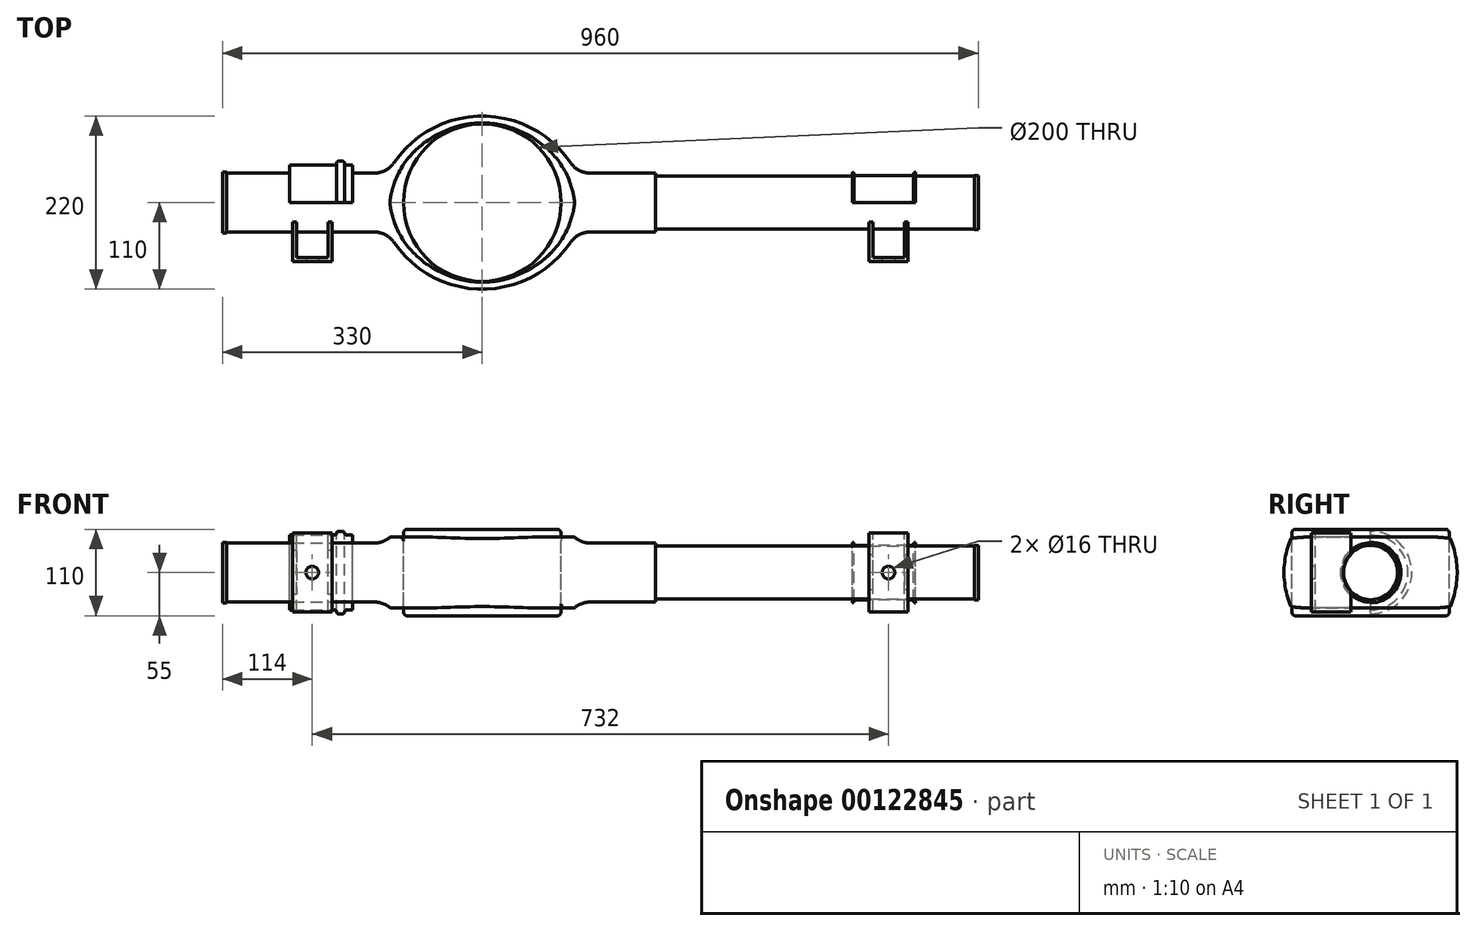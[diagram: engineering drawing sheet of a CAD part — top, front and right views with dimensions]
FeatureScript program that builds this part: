
annotation { "Feature Type Name" : "Feature", "Feature Type Description" : "" }
export const myFeature = defineFeature(function(context is Context, id is Id, definition is map)
    precondition{}
    {
        {
            var Q0;
            Q0=qCreatedBy(makeId("Front.planeOp"),FACE);
            var sketch = newSketch(context, id + "F0", { "sketchPlane" : qUnion([Q0])});
            skLineSegment(sketch, "E0", {"start": v(0, 0) * mm, "end": v(480, 0) * mm, "construction": true});
            skLineSegment(sketch, "E1", {"start": v(0, 0) * mm, "end": v(-480, 0) * mm, "construction": true});
            skLineSegment(sketch, "E2", {"start": v(-480, 0) * mm, "end": v(-480, 38.5) * mm});
            skLineSegment(sketch, "E3", {"start": v(-480, 38.5) * mm, "end": v(-475, 38.5) * mm});
            skLineSegment(sketch, "E4", {"start": v(-475, 38.5) * mm, "end": v(-475, 37.5) * mm});
            skLineSegment(sketch, "E5", {"start": v(-475, 37.5) * mm, "end": v(-395, 37.5) * mm});
            skLineSegment(sketch, "E6", {"start": v(-395, 37.5) * mm, "end": v(-395, 47.5) * mm});
            skLineSegment(sketch, "E7", {"start": v(-395, 47.5) * mm, "end": v(-337.5, 47.5) * mm});
            skLineSegment(sketch, "E8", {"start": v(-335, 50) * mm, "end": v(-335, 50) * mm});
            skLineSegment(sketch, "E9", {"start": v(-332.5, 52.5) * mm, "end": v(-327.5, 52.5) * mm});
            skLineSegment(sketch, "E10", {"start": v(-325, 50) * mm, "end": v(-325, 50) * mm});
            skLineSegment(sketch, "E11", {"start": v(-322.5, 47.5) * mm, "end": v(-315, 47.5) * mm});
            skLineSegment(sketch, "E12", {"start": v(-315, 47.5) * mm, "end": v(-315, 37.5) * mm});
            skLineSegment(sketch, "E13", {"start": v(-315, 37.5) * mm, "end": v(-286.93, 37.5) * mm});
            skLineSegment(sketch, "E14", {"start": v(-270, 37.5) * mm, "end": v(-30, 37.5) * mm});
            skPoint(sketch, "E15", {"position": v(-150, 110) * mm});
            skArc(sketch, "E16", {"start": v(-37.88, 50.64) * mm, "mid": v(-150, 110) * mm, "end": v(-262.12, 50.64) * mm});
            skPoint(sketch, "E17.visualSharp", {"position": v(-270, 37.5) * mm});
            skArc(sketch, "E17.filletArc", {"start": v(-286.93, 37.5) * mm, "mid": v(-272.9, 40.99) * mm, "end": v(-262.12, 50.64) * mm});
            skLineSegment(sketch, "E18", {"start": v(-13.07, 37.5) * mm, "end": v(70, 37.5) * mm});
            skLineSegment(sketch, "E19", {"start": v(70, 38) * mm, "end": v(70, 37.5) * mm});
            skLineSegment(sketch, "E20", {"start": v(480, 0) * mm, "end": v(480, 33.5) * mm});
            skLineSegment(sketch, "E21", {"start": v(475, 33.5) * mm, "end": v(400, 33.5) * mm});
            skLineSegment(sketch, "E22", {"start": v(400, 33.5) * mm, "end": v(400, 38.5) * mm});
            skLineSegment(sketch, "E23", {"start": v(400, 38.5) * mm, "end": v(400, 38.5) * mm});
            skLineSegment(sketch, "E24", {"start": v(398, 36.5) * mm, "end": v(398, 36.5) * mm});
            skLineSegment(sketch, "E25", {"start": v(396, 34.5) * mm, "end": v(324, 34.5) * mm});
            skLineSegment(sketch, "E26", {"start": v(322, 36.5) * mm, "end": v(322, 36.5) * mm});
            skLineSegment(sketch, "E27", {"start": v(320, 38.5) * mm, "end": v(320, 38.5) * mm});
            skLineSegment(sketch, "E28", {"start": v(320, 38.5) * mm, "end": v(320, 33.5) * mm});
            skLineSegment(sketch, "E29", {"start": v(73, 33.5) * mm, "end": v(320, 33.5) * mm});
            skLineSegment(sketch, "E30", {"start": v(-395, 37.5) * mm, "end": v(-315, 37.5) * mm});
            skLineSegment(sketch, "E31", {"start": v(320, 33.5) * mm, "end": v(400, 33.5) * mm});
            skLineSegment(sketch, "E32", {"start": v(480, 33.5) * mm, "end": v(480, 34.5) * mm});
            skLineSegment(sketch, "E33", {"start": v(480, 34.5) * mm, "end": v(475, 34.5) * mm});
            skLineSegment(sketch, "E34", {"start": v(475, 34.5) * mm, "end": v(475, 33.5) * mm});
            skPoint(sketch, "E35.visualSharp", {"position": v(-30, 37.5) * mm});
            skArc(sketch, "E35.filletArc", {"start": v(-37.88, 50.64) * mm, "mid": v(-27.1, 40.99) * mm, "end": v(-13.07, 37.5) * mm});
            skPoint(sketch, "E36.visualSharp", {"position": v(70, 33.5) * mm});
            skPoint(sketch, "E37.visualSharp", {"position": v(-335, 47.5) * mm});
            skArc(sketch, "E37.filletArc", {"start": v(-337.5, 47.5) * mm, "mid": v(-335.73, 48.23) * mm, "end": v(-335, 50) * mm});
            skPoint(sketch, "E38.visualSharp", {"position": v(-335, 52.5) * mm});
            skArc(sketch, "E38.filletArc", {"start": v(-332.5, 52.5) * mm, "mid": v(-334.27, 51.77) * mm, "end": v(-335, 50) * mm});
            skPoint(sketch, "E39.visualSharp", {"position": v(-325, 52.5) * mm});
            skArc(sketch, "E39.filletArc", {"start": v(-325, 50) * mm, "mid": v(-325.73, 51.77) * mm, "end": v(-327.5, 52.5) * mm});
            skPoint(sketch, "E40.visualSharp", {"position": v(-325, 47.5) * mm});
            skArc(sketch, "E40.filletArc", {"start": v(-325, 50) * mm, "mid": v(-324.27, 48.23) * mm, "end": v(-322.5, 47.5) * mm});
            skPoint(sketch, "E41.visualSharp", {"position": v(322, 34.5) * mm});
            skArc(sketch, "E41.filletArc", {"start": v(322, 36.5) * mm, "mid": v(322.59, 35.09) * mm, "end": v(324, 34.5) * mm});
            skPoint(sketch, "E42.visualSharp", {"position": v(398, 34.5) * mm});
            skArc(sketch, "E42.filletArc", {"start": v(396, 34.5) * mm, "mid": v(397.41, 35.09) * mm, "end": v(398, 36.5) * mm});
            skPoint(sketch, "E43.visualSharp", {"position": v(322, 38.5) * mm});
            skArc(sketch, "E43.filletArc", {"start": v(322, 36.5) * mm, "mid": v(321.41, 37.91) * mm, "end": v(320, 38.5) * mm});
            skPoint(sketch, "E44.visualSharp", {"position": v(398, 38.5) * mm});
            skArc(sketch, "E44.filletArc", {"start": v(400, 38.5) * mm, "mid": v(398.59, 37.91) * mm, "end": v(398, 36.5) * mm});
            skLineSegment(sketch, "E45", {"start": v(-480, 0) * mm, "end": v(480, 0) * mm});
            skLineSegment(sketch, "E46", {"start": v(-480, 0) * mm, "end": v(-552.56, 0) * mm, "construction": true});
            skLineSegment(sketch, "E47", {"start": v(70, 37.5) * mm, "end": v(70, 36.5) * mm});
            skLineSegment(sketch, "E48", {"start": v(73, 33.5) * mm, "end": v(73, 33.5) * mm});
            skArc(sketch, "E49.filletArc", {"start": v(70, 36.5) * mm, "mid": v(70.88, 34.38) * mm, "end": v(73, 33.5) * mm});
            skSolve(sketch);
        }
        {
            var Q0;
            Q0=makeQuery(id+"F0.imprint","IMPRINT",FACE,{"disambiguationData":[TD([[makeQuery(id+"F0.imprint","IMPRINT",EDGE,{"derivedFrom":sQuery(id+"F0.wireOp",EDGE,"E2")}),-1.0]])]});
            var Q1;
            Q1=sQuery(id+"F0.wireOp",EDGE,"E45");
            revolve(context, id + "F1", {"entities" : qUnion([Q0]), "axis" : qUnion([Q1]), "revolveType" : RevolveType.FULL});
        }
        {
            var Q0;
            Q0=makeQuery(id+"F0.imprint","IMPRINT",FACE,{"disambiguationData":[TD([[makeQuery(id+"F0.imprint","IMPRINT",EDGE,{"derivedFrom":sQuery(id+"F0.wireOp",EDGE,"E6")}),-1.0]])]});
            var Q1;
            Q1=makeQuery(id+"F0.imprint","IMPRINT",FACE,{"disambiguationData":[TD([[makeQuery(id+"F0.imprint","IMPRINT",EDGE,{"derivedFrom":sQuery(id+"F0.wireOp",EDGE,"E22")}),1.0]])]});
            var Q2;
            Q2=sQuery(id+"F0.wireOp",EDGE,"E46");
            revolve(context, id + "F2", {"operationType" : NewBodyOperationType.ADD, "entities" : qUnion([Q0, Q1]), "axis" : qUnion([Q2]), "revolveType" : RevolveType.ONE_DIRECTION, "angle" : 180 * degree});
        }
        {
            var Q0;
            Q0=qCreatedBy(makeId("Top.planeOp"),FACE);
            cPlane(context, id + "F3", {"entities" : qUnion([Q0]), "cplaneType" : CPlaneType.OFFSET, "offset" : 110 * mm, "width" : 150 * mm, "height" : 150 * mm});
        }
        {
            var Q0;
            Q0=qCreatedBy(id+"F3.planeOp",FACE);
            var sketch = newSketch(context, id + "F4", { "sketchPlane" : qUnion([Q0])});
            skLineSegment(sketch, "E50", {"start": v(0, 0) * mm, "end": v(-150, 0) * mm});
            skCircle(sketch, "E51", {"center": v(-150, 0) * mm, "radius": 100 * mm});
            skSolve(sketch);
        }
        {
            var Q0;
            Q0 = qSketchRegion(id + "F4", true);
            extrude(context, id + "F5", {"entities" : qUnion([Q0]), "operationType" : NewBodyOperationType.REMOVE, "oppositeDirection" : true, "depth" : 220 * mm});
        }
        {
            var Q0;
            Q0=qCreatedBy(makeId("Right.planeOp"),FACE);
            cPlane(context, id + "F6", {"entities" : qUnion([Q0]), "cplaneType" : CPlaneType.OFFSET, "offset" : 270 * mm, "oppositeDirection" : true, "width" : 150 * mm, "height" : 150 * mm});
        }
        {
            var Q0;
            Q0=qCreatedBy(id+"F6.planeOp",FACE);
            var sketch = newSketch(context, id + "F7", { "sketchPlane" : qUnion([Q0])});
            skLineSegment(sketch, "E52", {"start": v(0, 0) * mm, "end": v(-110, 0) * mm});
            skLineSegment(sketch, "E53", {"start": v(-110, 0) * mm, "end": v(-110, 45) * mm});
            skLineSegment(sketch, "E54", {"start": v(-110, 45) * mm, "end": v(110, 45) * mm});
            skLineSegment(sketch, "E55", {"start": v(110, 45) * mm, "end": v(110, -45) * mm});
            skLineSegment(sketch, "E56", {"start": v(110, -45) * mm, "end": v(-110, -45) * mm});
            skLineSegment(sketch, "E57", {"start": v(-110, -45) * mm, "end": v(-110, 0) * mm});
            skLineSegment(sketch, "E58", {"start": v(110, 45) * mm, "end": v(110, 66) * mm});
            skLineSegment(sketch, "E59", {"start": v(110, 66) * mm, "end": v(-110, 66) * mm});
            skLineSegment(sketch, "E60", {"start": v(-110, 66) * mm, "end": v(-110, 45) * mm});
            skLineSegment(sketch, "E61", {"start": v(110, -45) * mm, "end": v(110, -66) * mm});
            skLineSegment(sketch, "E62", {"start": v(110, -66) * mm, "end": v(-110, -66) * mm});
            skLineSegment(sketch, "E63", {"start": v(-110, -66) * mm, "end": v(-110, -45) * mm});
            skSolve(sketch);
        }
        {
            var Q0;
            Q0=makeQuery(id+"F7.imprint","IMPRINT",FACE,{"disambiguationData":[TD([[makeQuery(id+"F7.imprint","IMPRINT",EDGE,{"derivedFrom":sQuery(id+"F7.wireOp",EDGE,"E54")}),1.0]])]});
            var Q1;
            Q1=makeQuery(id+"F7.imprint","IMPRINT",FACE,{"disambiguationData":[TD([[makeQuery(id+"F7.imprint","IMPRINT",EDGE,{"derivedFrom":sQuery(id+"F7.wireOp",EDGE,"E56")}),1.0]])]});
            extrude(context, id + "F8", {"entities" : qUnion([Q0, Q1]), "operationType" : NewBodyOperationType.REMOVE, "depth" : 240 * mm});
        }
        {
            var Q0;
            Q0=qCreatedBy(makeId("Top.planeOp"),FACE);
            cPlane(context, id + "F9", {"entities" : qUnion([Q0]), "cplaneType" : CPlaneType.OFFSET, "offset" : 55 * mm, "width" : 150 * mm, "height" : 150 * mm});
        }
        {
            var Q0;
            Q0=qCreatedBy(id+"F9.planeOp",FACE);
            var sketch = newSketch(context, id + "F10", { "sketchPlane" : qUnion([Q0])});
            skLineSegment(sketch, "E64", {"start": v(0, 0) * mm, "end": v(-150, 0) * mm});
            skCircle(sketch, "E65", {"center": v(-150, 0) * mm, "radius": 100 * mm});
            skSolve(sketch);
        }
        {
            var Q0;
            Q0 = qSketchRegion(id + "F10", true);
            extrude(context, id + "F11", {"entities" : qUnion([Q0]), "oppositeDirection" : true, "depth" : 110 * mm});
        }
        {
            var Q0;
            Q0=makeQuery(id+"F11.opExtrude","CAP_EDGE",EDGE,{"disambiguationData":[OSD([sQuery(id+"F10.wireOp",EDGE,"E65")])],"isStart":true});
            var Q1;
            Q1=makeQuery(id+"F8.boolean.opBoolean","INTERSECT",EDGE,{"derivedFrom":[makeQuery(id+"F5.boolean.opBoolean","COPY",FACE,{"derivedFrom":makeQuery(id+"F5.opExtrude","SWEPT_FACE",FACE,{"disambiguationData":[OSD([sQuery(id+"F4.wireOp",EDGE,"E51")])]})}),makeQuery(id+"F8.opExtrude","SWEPT_FACE",FACE,{"disambiguationData":[OSD([sQuery(id+"F7.wireOp",EDGE,"E54")])]})]});
            fillet(context, id + "F12", {"entities" : qUnion([Q0, Q1]), "radius" : 5 * mm, "tangentPropagation" : true, "allowEdgeOverflow" : false});
        }
        {
            var Q0;
            Q0=makeQuery(id+"F11.opExtrude","CAP_EDGE",EDGE,{"disambiguationData":[OSD([sQuery(id+"F10.wireOp",EDGE,"E65")])],"isStart":false});
            var Q1;
            Q1=makeQuery(id+"F8.boolean.opBoolean","INTERSECT",EDGE,{"derivedFrom":[makeQuery(id+"F5.boolean.opBoolean","COPY",FACE,{"derivedFrom":makeQuery(id+"F5.opExtrude","SWEPT_FACE",FACE,{"disambiguationData":[OSD([sQuery(id+"F4.wireOp",EDGE,"E51")])]})}),makeQuery(id+"F8.opExtrude","SWEPT_FACE",FACE,{"disambiguationData":[OSD([sQuery(id+"F7.wireOp",EDGE,"E56")])]})]});
            fillet(context, id + "F13", {"entities" : qUnion([Q0, Q1]), "radius" : 5 * mm, "tangentPropagation" : true, "allowEdgeOverflow" : false});
        }
        {
            var Q0;
            Q0=qCreatedBy(makeId("Top.planeOp"),FACE);
            cPlane(context, id + "F14", {"entities" : qUnion([Q0]), "cplaneType" : CPlaneType.OFFSET, "offset" : 50 * mm, "width" : 150 * mm, "height" : 150 * mm});
        }
        {
            var Q0;
            Q0=qCreatedBy(id+"F14.planeOp",FACE);
            var sketch = newSketch(context, id + "F15", { "sketchPlane" : qUnion([Q0])});
            skLineSegment(sketch, "E66", {"start": v(0, 0) * mm, "end": v(391, 0) * mm});
            skLineSegment(sketch, "E67", {"start": v(391, 0) * mm, "end": v(391, -25.04) * mm});
            skLineSegment(sketch, "E68", {"start": v(391, -25.04) * mm, "end": v(341, -25.04) * mm});
            skLineSegment(sketch, "E69", {"start": v(341, -25.04) * mm, "end": v(341, -75.04) * mm});
            skLineSegment(sketch, "E70", {"start": v(341, -75.04) * mm, "end": v(391, -75.04) * mm});
            skLineSegment(sketch, "E71", {"start": v(391, -75.04) * mm, "end": v(391, -25.04) * mm});
            skLineSegment(sketch, "E72.0", {"start": v(386, -70.04) * mm, "end": v(386, -25.04) * mm});
            skLineSegment(sketch, "E72.1", {"start": v(346, -70.04) * mm, "end": v(386, -70.04) * mm});
            skLineSegment(sketch, "E72.2", {"start": v(346, -25.04) * mm, "end": v(346, -70.04) * mm});
            skLineSegment(sketch, "E73", {"start": v(0, 175.63) * mm, "end": v(0, -175.61) * mm, "construction": true});
            skLineSegment(sketch, "E74.MirrorCS", {"start": v(-341, -75.04) * mm, "end": v(-391, -75.04) * mm});
            skLineSegment(sketch, "E75.MirrorCS", {"start": v(-346, -70.04) * mm, "end": v(-386, -70.04) * mm});
            skLineSegment(sketch, "E76.MirrorCS", {"start": v(-386, -70.04) * mm, "end": v(-386, -25.04) * mm});
            skLineSegment(sketch, "E77.MirrorCS", {"start": v(-391, -75.04) * mm, "end": v(-391, -25.04) * mm});
            skLineSegment(sketch, "E78.MirrorCS", {"start": v(-341, -25.04) * mm, "end": v(-341, -75.04) * mm});
            skLineSegment(sketch, "E79.MirrorCS", {"start": v(-346, -25.04) * mm, "end": v(-346, -70.04) * mm});
            skLineSegment(sketch, "E80.MirrorCS", {"start": v(-391, -25.04) * mm, "end": v(-341, -25.04) * mm});
            skSolve(sketch);
        }
        {
            var Q0;
            {var subQ0=sQuery(id+"F15.wireOp",EDGE,"E69");Q0=makeQuery(id+"F15.imprint","IMPRINT",FACE,{"disambiguationData":[TD([[makeQuery(id+"F15.imprint","IMPRINT",EDGE,{"derivedFrom":subQ0}),1.0]])]});}
            var Q1;
            Q1=makeQuery(id+"F15.imprint","IMPRINT",FACE,{"disambiguationData":[TD([[makeQuery(id+"F15.imprint","IMPRINT",EDGE,{"derivedFrom":sQuery(id+"F15.wireOp",EDGE,"E74.MirrorCS")}),-1.0]])]});
            extrude(context, id + "F16", {"entities" : qUnion([Q0, Q1]), "operationType" : NewBodyOperationType.ADD, "oppositeDirection" : true, "depth" : 100 * mm});
        }
        {
            var Q0;
            Q0=qCreatedBy(makeId("Front.planeOp"),FACE);
            cPlane(context, id + "F17", {"entities" : qUnion([Q0]), "cplaneType" : CPlaneType.OFFSET, "offset" : 76 * mm, "width" : 150 * mm, "height" : 150 * mm});
        }
        {
            var Q0;
            Q0=qCreatedBy(id+"F17.planeOp",FACE);
            var sketch = newSketch(context, id + "F18", { "sketchPlane" : qUnion([Q0])});
            skPoint(sketch, "E81", {"position": v(-366, 0) * mm});
            skPoint(sketch, "E82", {"position": v(366, 0) * mm});
            skCircle(sketch, "E83", {"center": v(-366, 0) * mm, "radius": 8 * mm});
            skCircle(sketch, "E84", {"center": v(366, 0) * mm, "radius": 8 * mm});
            skSolve(sketch);
        }
        {
            var Q0;
            Q0 = qSketchRegion(id + "F18", true);
            extrude(context, id + "F19", {"entities" : qUnion([Q0]), "operationType" : NewBodyOperationType.REMOVE, "oppositeDirection" : true, "depth" : 6 * mm});
        }
    });
